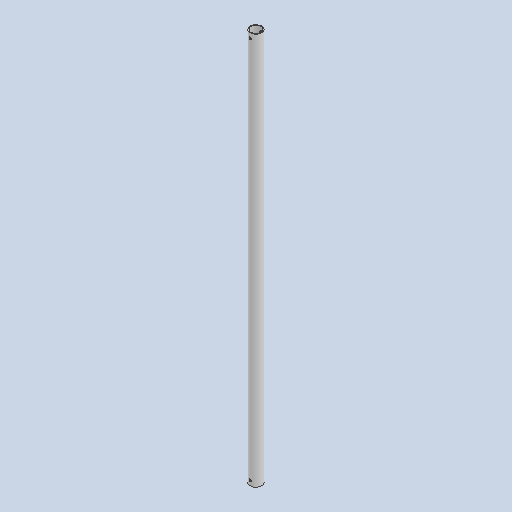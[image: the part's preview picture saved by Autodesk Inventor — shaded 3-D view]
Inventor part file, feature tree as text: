
AUTODESK INVENTOR PART (.ipt)
format: ipt  version: 2022 (Build 260153000, 153)  size: 174,080 bytes
history: native  units: mm
features: extrude x2, sketch x2
ambient origin geometry x8: Origin, YZ Plane, XZ Plane, XY Plane, X Axis, Y Axis, Z Axis, Center Point
bodies: Body1 (feature_tree)
feature tree (4):
  extrude  "Extrusion5"  Depth=15.0mm
  extrude  "Extrusion6"  Depth=6.0mm TaperAngle=0.0deg
  sketch  "Sketch2"  dims[d31=34.456mm d91=15.0mm]
  sketch  "Sketch3"  dims[d92=13.0mm d93=500.0mm d94=0.0mm d95=6.0mm d96=3.0mm d97=20.0mm d98=10.0mm d99=0.0mm d100=0.0mm d101=6.0mm d102=3.0mm]
